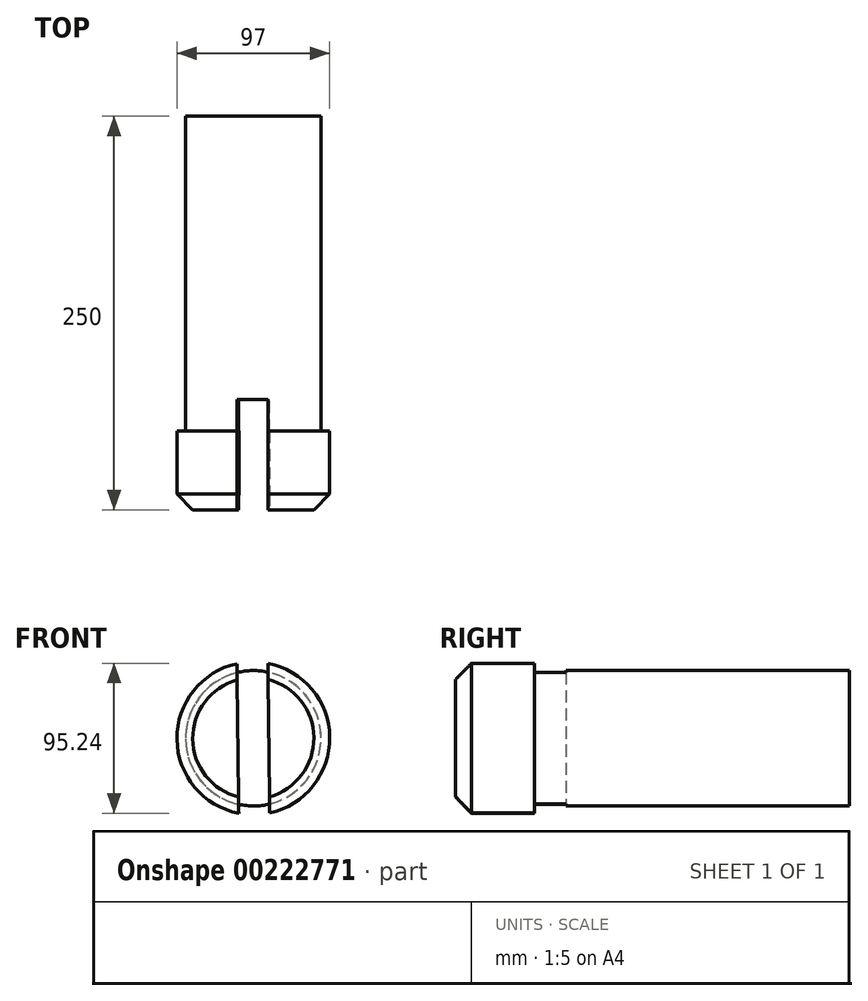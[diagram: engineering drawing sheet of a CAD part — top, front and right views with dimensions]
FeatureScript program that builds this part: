
annotation { "Feature Type Name" : "Feature", "Feature Type Description" : "" }
export const myFeature = defineFeature(function(context is Context, id is Id, definition is map)
    precondition{}
    {
        {
            var Q0;
            Q0=qCreatedBy(makeId("Front.planeOp"),FACE);
            var sketch = newSketch(context, id + "F0", { "sketchPlane" : qUnion([Q0])});
            skCircle(sketch, "E0", {"center": v(0, 0) * mm, "radius": 48.5 * mm});
            skCircle(sketch, "E1.0", {"center": v(0, 0) * mm, "radius": 43 * mm});
            skSolve(sketch);
        }
        {
            var Q0;
            Q0=makeQuery(id+"F0.imprint","IMPRINT",FACE,{"disambiguationData":[TD([[makeQuery(id+"F0.imprint","IMPRINT",EDGE,{"derivedFrom":sQuery(id+"F0.wireOp",EDGE,"E0")}),1.0]])]});
            var Q1;
            Q1=makeQuery(id+"F0.imprint","IMPRINT",FACE,{"disambiguationData":[TD([[makeQuery(id+"F0.imprint","IMPRINT",EDGE,{"derivedFrom":sQuery(id+"F0.wireOp",EDGE,"E1.0")}),1.0]])]});
            extrude(context, id + "F1", {"entities" : qUnion([Q0, Q1]), "depth" : 250 * mm});
        }
        {
            var Q0;
            Q0=makeQuery(id+"F0.imprint","IMPRINT",FACE,{"disambiguationData":[TD([[makeQuery(id+"F0.imprint","IMPRINT",EDGE,{"derivedFrom":sQuery(id+"F0.wireOp",EDGE,"E0")}),1.0]])]});
            extrude(context, id + "F2", {"entities" : qUnion([Q0]), "operationType" : NewBodyOperationType.REMOVE, "depth" : 200 * mm});
        }
        {
            var Q0;
            Q0=makeQuery(id+"F1.opExtrude","CAP_FACE",FACE,{"disambiguationData":[OSD([sQuery(id+"F0.wireOp",EDGE,"E0")])],"isStart":false});
            var sketch = newSketch(context, id + "F3", { "sketchPlane" : qUnion([Q0])});
            skLineSegment(sketch, "E2.left", {"start": v(9.22, 47.62) * mm, "end": v(10.45, -53.94) * mm});
            skLineSegment(sketch, "E2.right", {"start": v(-10.45, 53.94) * mm, "end": v(-9.22, -47.62) * mm});
            skPoint(sketch, "E2.middle", {"position": v(0, 0) * mm});
            skSolve(sketch);
        }
        {
            var Q0;
            {var subQ0=sQuery(id+"F3.wireOp",EDGE,"E2.left");Q0=makeQuery(id+"F3.imprint","IMPRINT",FACE,{"disambiguationData":[TD([[makeQuery(id+"F3.imprint","IMPRINT",EDGE,{"derivedFrom":subQ0}),-1.0]])]});}
            extrude(context, id + "F4", {"entities" : qUnion([Q0]), "operationType" : NewBodyOperationType.REMOVE, "oppositeDirection" : true, "depth" : 70 * mm});
        }
        {
            var Q0;
            {var subQ0=sQuery(id+"F0.wireOp",EDGE,"E0");Q0=makeQuery(id+"F4.boolean.opBoolean","SPLIT",EDGE,{"disambiguationData":[TD([makeQuery(id+"F4.opExtrude","SWEPT_FACE",FACE,{"disambiguationData":[OSD([sQuery(id+"F3.wireOp",EDGE,"E2.right")])]})])],"derivedFrom":makeQuery(id+"F1.opExtrude","CAP_EDGE",EDGE,{"disambiguationData":[OSD([subQ0])],"isStart":false})});}
            var Q1;
            {var subQ0=sQuery(id+"F0.wireOp",EDGE,"E0");Q1=makeQuery(id+"F4.boolean.opBoolean","SPLIT",EDGE,{"disambiguationData":[TD([makeQuery(id+"F4.opExtrude","SWEPT_FACE",FACE,{"disambiguationData":[OSD([sQuery(id+"F3.wireOp",EDGE,"E2.left")])]})])],"derivedFrom":makeQuery(id+"F1.opExtrude","CAP_EDGE",EDGE,{"disambiguationData":[OSD([subQ0])],"isStart":false})});}
            var Q2;
            {var subQ0=sQuery(id+"F0.wireOp",EDGE,"E0");Q2=makeQuery(id+"F4.boolean.opBoolean","SPLIT",EDGE,{"disambiguationData":[TD([makeQuery(id+"F4.opExtrude","SWEPT_FACE",FACE,{"disambiguationData":[OSD([sQuery(id+"F3.wireOp",EDGE,"E2.left")])]})])],"derivedFrom":makeQuery(id+"F2.boolean.opBoolean","COPY",EDGE,{"derivedFrom":makeQuery(id+"F2.opExtrude","CAP_EDGE",EDGE,{"disambiguationData":[OSD([subQ0])],"isStart":false})})});}
            var Q3;
            {var subQ0=sQuery(id+"F0.wireOp",EDGE,"E0");Q3=makeQuery(id+"F4.boolean.opBoolean","SPLIT",EDGE,{"disambiguationData":[TD([makeQuery(id+"F4.opExtrude","SWEPT_FACE",FACE,{"disambiguationData":[OSD([sQuery(id+"F3.wireOp",EDGE,"E2.right")])]})])],"derivedFrom":makeQuery(id+"F2.boolean.opBoolean","COPY",EDGE,{"derivedFrom":makeQuery(id+"F2.opExtrude","CAP_EDGE",EDGE,{"disambiguationData":[OSD([subQ0])],"isStart":false})})});}
            chamfer(context, id + "F5", {"entities" : qUnion([Q0, Q1, Q2, Q3]), "width" : 10 * mm, "tangentPropagation" : true});
        }
    });
